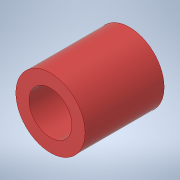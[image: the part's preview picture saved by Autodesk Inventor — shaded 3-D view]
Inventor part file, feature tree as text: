
AUTODESK INVENTOR PART (.ipt)
format: ipt  version: 2022.3 (Build 263350000, 350)  size: 107,520 bytes
history: native  units: in
note: dims shown in document units (in); Inventor stores cm internally (conversion verified against a paired STEP export)
features: sketch x1, extrude x1, hole x1
ambient origin geometry x8: Origin, YZ Plane, XZ Plane, XY Plane, X Axis, Y Axis, Z Axis, Center Point
bodies: Solid1 (feature_tree)
feature tree (3):
  sketch  "Sketch1"  dims[d1=1.0in d2=0.0in d3=0.5433in d4=0.75in d5=0.385in d6=0.25in d7=0.5635in d8=1.0in d9=0.8108in d10=0.875in]
  extrude  "Extrusion1"  TaperAngle=0.0deg  [1 undecoded]
  hole  "Hole1"  [1 undecoded]
note: 2 required parameter values undecoded (feature->parameter linkage not recoverable at this tier; creation-order binding heuristic only, values carry confidence <= 0.55)
